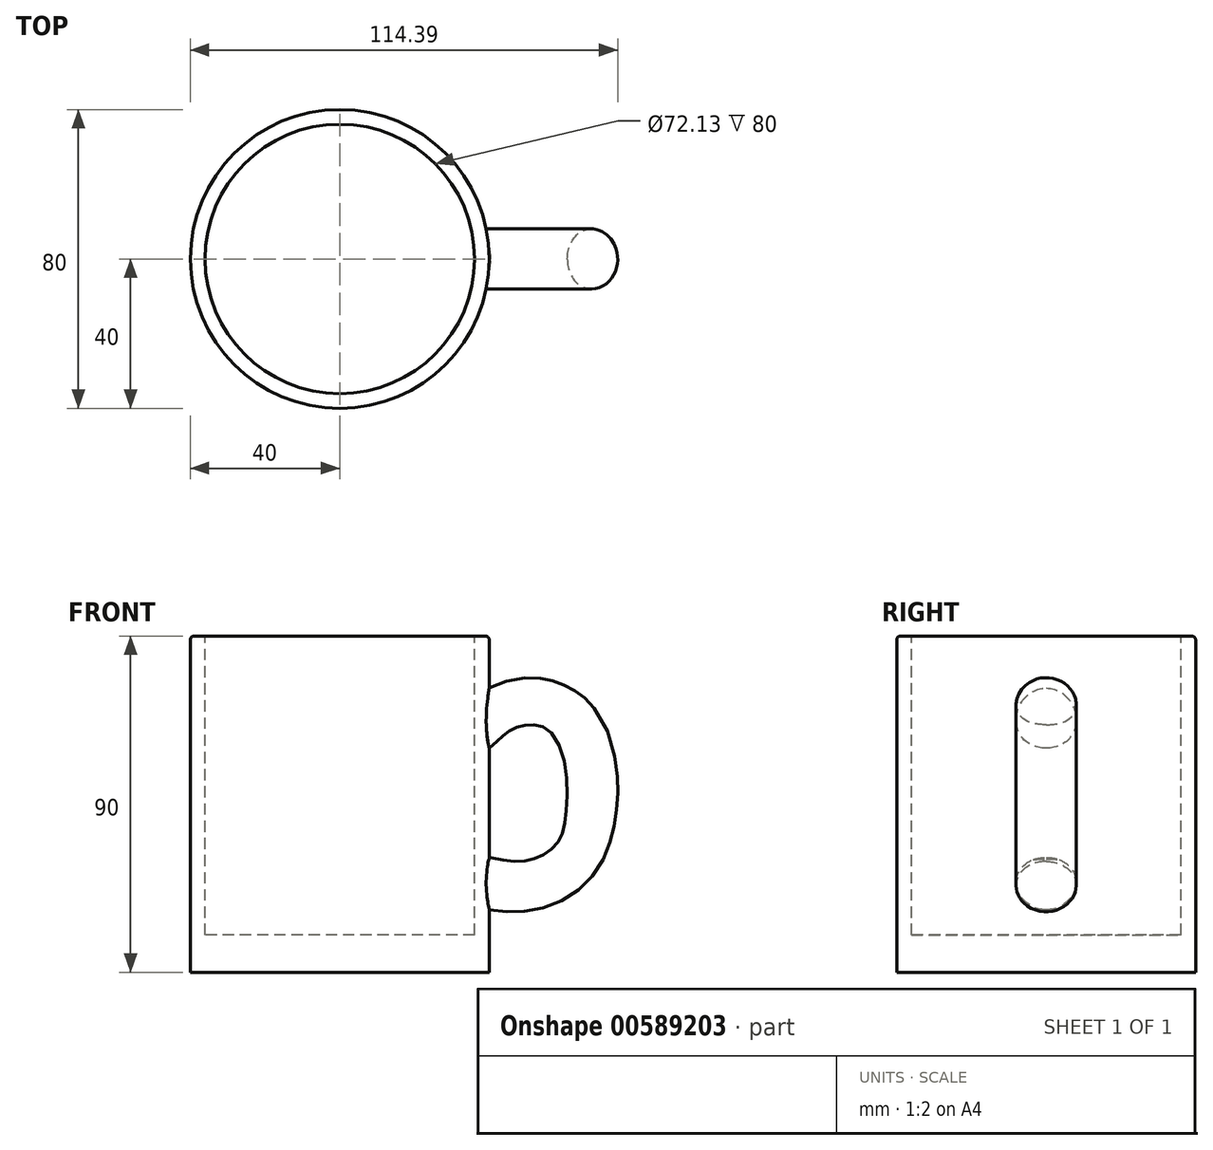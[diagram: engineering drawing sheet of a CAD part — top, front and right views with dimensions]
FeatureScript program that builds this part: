
annotation { "Feature Type Name" : "Feature", "Feature Type Description" : "" }
export const myFeature = defineFeature(function(context is Context, id is Id, definition is map)
    precondition{}
    {
        {
            var Q0;
            Q0=qCreatedBy(makeId("Top.planeOp"),FACE);
            var sketch = newSketch(context, id + "F0", { "sketchPlane" : qUnion([Q0])});
            skCircle(sketch, "E0", {"center": v(0, 0) * mm, "radius": 40 * mm});
            skSolve(sketch);
        }
        {
            var Q0;
            Q0=makeQuery(id+"F0.imprint","IMPRINT",FACE,{"disambiguationData":[TD([[makeQuery(id+"F0.imprint","IMPRINT",EDGE,{"derivedFrom":sQuery(id+"F0.wireOp",EDGE,"E0")}),1.0]])]});
            extrude(context, id + "F1", {"entities" : qUnion([Q0]), "depth" : 90 * mm, "offsetDistance" : 25 * mm});
        }
        {
            var Q0;
            Q0=qCreatedBy(makeId("Right.planeOp"),FACE);
            cPlane(context, id + "F2", {"entities" : qUnion([Q0]), "cplaneType" : CPlaneType.OFFSET, "offset" : 40 * mm, "width" : 150 * mm, "height" : 150 * mm});
        }
        {
            var Q0;
            Q0=qCreatedBy(makeId("Front.planeOp"),FACE);
            var sketch = newSketch(context, id + "F3", { "sketchPlane" : qUnion([Q0])});
            skFitSpline(sketch, "E1", {"points": [v(34.83, 66.15) * mm, v(48.78, 73.01) * mm, v(64.85, 65.4) * mm, v(65.15, 32.31) * mm, v(48.82, 22) * mm, v(33.52, 23.95) * mm], "startDerivative": vector(73.58, 52.68) * mm, "endDerivative": vector(-84.23, 21.22) * mm});
            skSolve(sketch);
        }
        {
            var Q0;
            Q0=qCreatedBy(id+"F2.planeOp",FACE);
            var sketch = newSketch(context, id + "F4", { "sketchPlane" : qUnion([Q0])});
            skCircle(sketch, "E2", {"center": v(0, 68.05) * mm, "radius": 8.05 * mm});
            skSolve(sketch);
        }
        {
            var Q0;
            Q0=makeQuery(id+"F4.imprint","IMPRINT",FACE,{"disambiguationData":[TD([[makeQuery(id+"F4.imprint","IMPRINT",EDGE,{"derivedFrom":sQuery(id+"F4.wireOp",EDGE,"E2")}),1.0]])]});
            var Q1;
            Q1=sQuery(id+"F3.wireOp",EDGE,"E1");
            sweep(context, id + "F5", {"operationType" : NewBodyOperationType.ADD, "profiles" : qUnion([Q0]), "path" : qUnion([Q1])});
        }
        {
            var Q0;
            Q0=makeQuery(id+"F1.opExtrude","CAP_FACE",FACE,{"disambiguationData":[OSD([sQuery(id+"F0.wireOp",EDGE,"E0")])],"isStart":false});
            var sketch = newSketch(context, id + "F6", { "sketchPlane" : qUnion([Q0])});
            skCircle(sketch, "E3", {"center": v(0, 0) * mm, "radius": 36.06 * mm});
            skSolve(sketch);
        }
        {
            var Q0;
            Q0=makeQuery(id+"F6.imprint","IMPRINT",FACE,{"disambiguationData":[TD([[makeQuery(id+"F6.imprint","IMPRINT",EDGE,{"derivedFrom":sQuery(id+"F6.wireOp",EDGE,"E3")}),1.0]])]});
            extrude(context, id + "F7", {"entities" : qUnion([Q0]), "operationType" : NewBodyOperationType.REMOVE, "oppositeDirection" : true, "depth" : 80 * mm, "offsetDistance" : 25 * mm});
        }
        {
            var Q0;
            Q0=makeQuery(id+"F1.opExtrude","CAP_EDGE",EDGE,{"disambiguationData":[OSD([sQuery(id+"F0.wireOp",EDGE,"E0")])],"isStart":false});
            fillet(context, id + "F8", {"entities" : qUnion([Q0]), "radius" : 1 * mm, "tangentPropagation" : true, "allowEdgeOverflow" : false});
        }
    });
